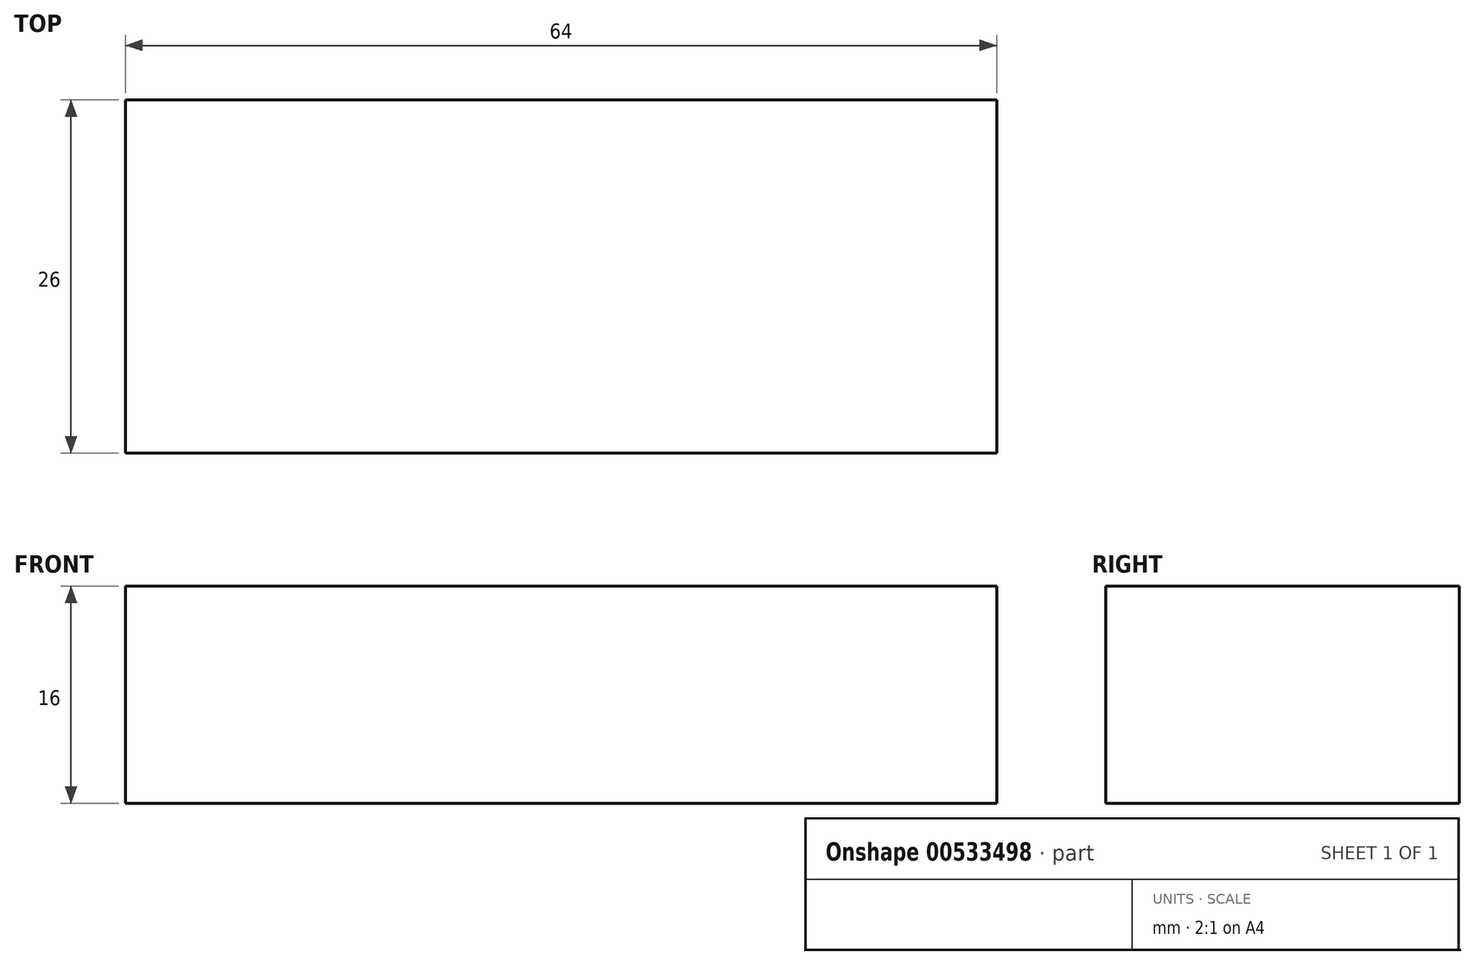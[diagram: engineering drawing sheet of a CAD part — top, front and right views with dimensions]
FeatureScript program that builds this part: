
annotation { "Feature Type Name" : "Feature", "Feature Type Description" : "" }
export const myFeature = defineFeature(function(context is Context, id is Id, definition is map)
    precondition{}
    {
        {
            var Q0;
            Q0=qCreatedBy(makeId("Top.planeOp"),FACE);
            var sketch = newSketch(context, id + "F0", { "sketchPlane" : qUnion([Q0])});
            skLineSegment(sketch, "E0.bottom", {"start": v(0, 0) * mm, "end": v(64, 0) * mm});
            skLineSegment(sketch, "E0.top", {"start": v(0, 26) * mm, "end": v(64, 26) * mm});
            skLineSegment(sketch, "E0.left", {"start": v(0, 0) * mm, "end": v(0, 26) * mm});
            skLineSegment(sketch, "E0.right", {"start": v(64, 0) * mm, "end": v(64, 26) * mm});
            skSolve(sketch);
        }
        {
            var Q0;
            Q0=qSketchRegion(id+"F0",true);
            extrude(context, id + "F1", {"entities" : qUnion([Q0]), "depth" : 16 * mm, "offsetDistance" : 25 * mm});
        }
    });
